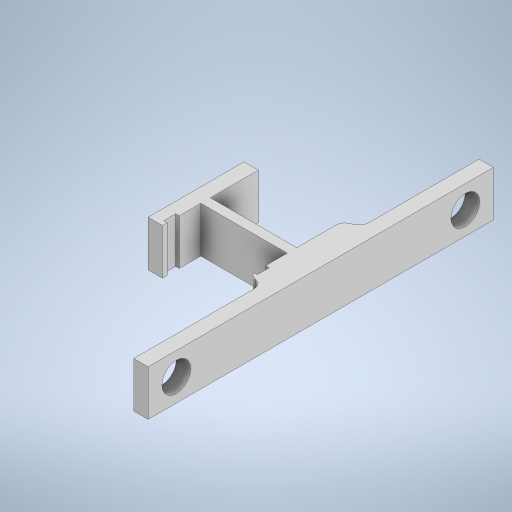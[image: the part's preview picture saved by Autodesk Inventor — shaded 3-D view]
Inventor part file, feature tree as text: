
AUTODESK INVENTOR PART (.ipt)
format: ipt  version: 2024 (Build 280153000, 153)  size: 300,544 bytes
history: native  units: in
note: dims shown in document units (in); Inventor stores cm internally (conversion verified against a paired STEP export)
features: extrude x2, sketch x2, fillet x1
ambient origin geometry x8: Origin, YZ Plane, XZ Plane, XY Plane, X Axis, Y Axis, Z Axis, Center Point
bodies: Solid1 (feature_tree)
feature tree (5):
  extrude  "Extrusion1"  Depth=0.1181in
  fillet  "Fillet1"  Radius=0.1181in
  extrude  "Extrusion2"  Depth=0.3937in
  sketch  "Sketch1"  dims[d0=0.0984in d1=0.1181in d2=0.1181in]
  sketch  "Sketch2"  dims[d3=0.3937in d4=0.3937in d5=0.0787in d6=0.1181in d8=0.0394in d9=0.315in d11=0.0295in d12=0.0295in d13=0.1181in d14=0.374in d15=0.0in d16=0.7087in d17=0.1181in d18=2.8346in d19=1.378in d20=0.0787in d21=0.2362in d22=0.2362in d23=0.374in d24=0.187in d25=0.187in d26=2.372in d27=2.8346in d28=0.2313in d29=0.0in d30=0.0in]
